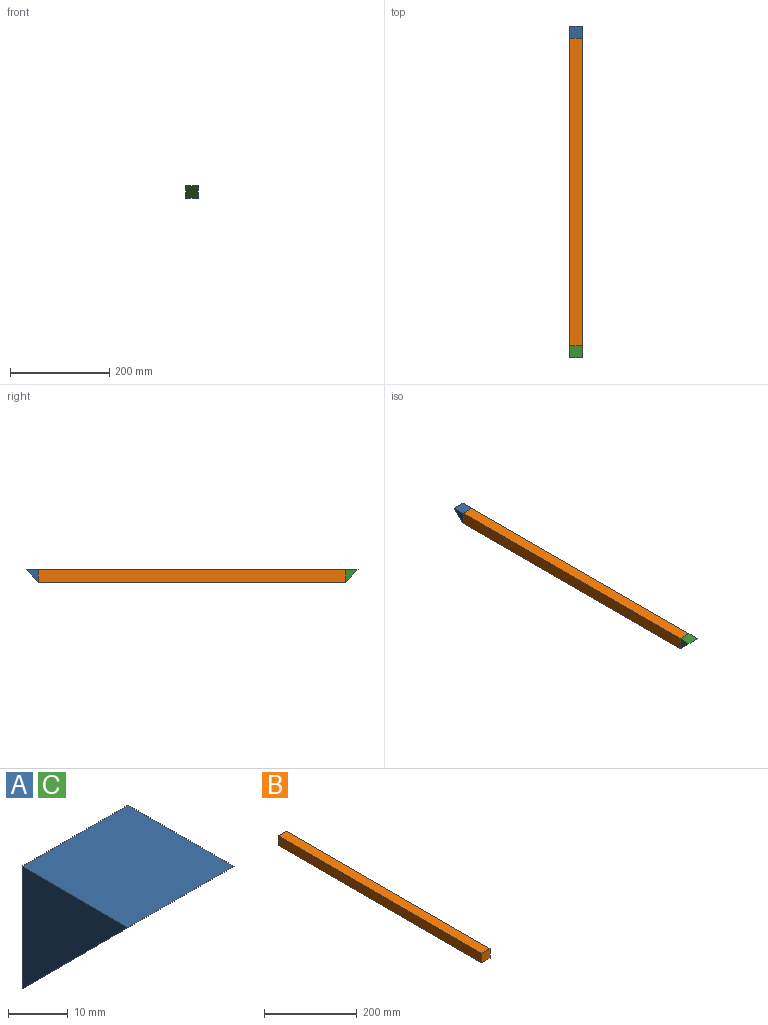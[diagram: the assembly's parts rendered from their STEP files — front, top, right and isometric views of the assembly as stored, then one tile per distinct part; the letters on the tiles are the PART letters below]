
ASSEMBLY  parts=3 mates=2
PART A: 5 faces, bbox 25x25x25 mm
  f0: plane 25x25mm, normal (-1,0,0), area 312.5mm2, adj f2,f3,f4
  f1: plane 25x25mm, normal (1,0,0), area 312.5mm2, adj f2,f3,f4
  f2: plane 25x25mm, normal (0,0,1), area 625mm2, adj f0,f1,f3,f4
  f3: plane 25x25mm, normal (0,1,0), area 625mm2, adj f0,f1,f2,f4
  f4: plane 25x25mm, normal (0,-0.71,-0.71), area 883.9mm2, adj f0,f1,f2,f3
PART B: 6 faces, bbox 25x620x25 mm
  f0: plane 620x25mm, normal (0,0,1), area 15500mm2, adj f1,f3,f4,f5
  f1: plane 620x25mm, normal (-1,0,0), area 15500mm2, adj f0,f2,f4,f5
  f2: plane 620x25mm, normal (0,0,-1), area 15500mm2, adj f1,f3,f4,f5
  f3: plane 620x25mm, normal (1,0,0), area 15500mm2, adj f0,f2,f4,f5
  f4: plane 25x25mm, normal (0,-1,0), area 625mm2, adj f0,f1,f2,f3
  f5: plane 25x25mm, normal (0,1,0), area 625mm2, adj f0,f1,f2,f3
PART C: same geometry as A
PLACE A rot(axis=(0,0,1),180deg) t=(-159.83,89.73,-101.98)mm
PLACE B t=(-159.83,89.73,-101.98)mm
PLACE C t=(-159.83,-530.27,-101.98)mm
MATE fastened A.f3 <-> B.f5  axis (0,-1,0) through (-159.83,89.73,-101.98)mm
MATE fastened C.f3 <-> B.f4  axis (0,1,0) through (-159.83,-530.27,-101.98)mm
